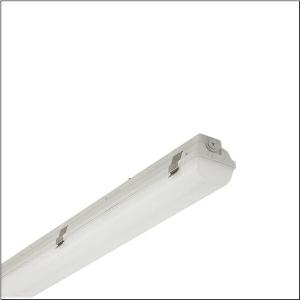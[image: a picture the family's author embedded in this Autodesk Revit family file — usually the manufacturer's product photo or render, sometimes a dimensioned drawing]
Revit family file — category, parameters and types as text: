
# Revit family: monsun_r__21_eco_51fj10ml45a_013e
name_source: partatom
category: Lighting Fixtures
units: mm (PartAtom-declared; Revit-internal decimal feet)

## family parameters
Cut with Voids When Loaded = No
Host = Face
Light Source = No
Part Type = Normal
Room Calculation Point = No
Round Connector Dimension = Use Diameter
Shared = No

## types (1)
- --- (1 x LED, 5000 lm, 36 W, 4000K)
    Apparent Load = 36 VA
    CIE Flux Codes = 41 70 89 90 100
    Color Rendering = 80
    Color Temperature = 4000K
    Default Elevation = 1800 mm
    Description = Monsun® 21 Eco, damp-proof luminaire, primary optical cover: diffuser, of PMMA, frosted, light emission: direct distribution, primary light characteristic: symmetric, installation type: suspended mounting, surface-mounted, LED, rated luminous flux: 5.000lm, luminous efficacy: 139lm/W, light colour: 840, colour temperature: 4000K, control gear: ON/OFF Multilumen, with terminal, 3-pole, max. 2.5mm², mains connection: 220..240V, AC, 50/60Hz, rated input power: 36W, housing, of glass-fibre reinforced polyester, light grey (RAL 7035), length: 1.277mm, width: 90mm, height: 95mm, clip for enclosure, of spring steel V2A, protection rating (complete): IP66, insulation class (complete): insulation class I (protective earthing), certification: CE, UKCA, protection symbol: D, impact resistance: IK02, permissible operating ambient temperature: -20..+35°C, corresponds to IFS (International Featured Standards) requirements for safety and quality in the food industry, contact your sales advisor before using the luminaires in applications with unclear chemical exposure, large temperature fluctuations or condensation-forming humidity, packaging unit: 1 piece
    Height = 103 mm
    Lamp = 1 x LED
    Lamp Light Flux = 5000 lm
    Lamp Power = 36 W
    Lamp count = 1
    Length = 1277 mm
    Luminous efficacy = 139 lm/W
    Manufacturer = Siteco
    ModVariant = No
    Model = 51FJ10ML45A
    Mounting Place = Ceiling
    Mounting Type = Surface mounted
    Number of Poles = 1
    OnlyDefault = Yes
    Power Factor = 1
    Product Name = Monsun® 21 Eco
    Product group = damp-proof luminaire
    ProductGroupID = 301
    Protection Class = Protection class I
    Protection Degree = IP 66
    RLX_Detail_Level = 1
    RLX_Emergency_Light_Flux = 0 lm
    RLX_Emergency_Type = 0
    RLX_Emergency_Type_DB = No
    RlxData = <blob elided: 34057 chars, md5=c035e402>
    Socket = socket
    Standby Power = 0 W
    System Light Flux = 5000 lm
    System Power = 36 W
    Type Comments = factory setting: luminous flux: 100 % | (ON | ON | ON | ON) | 350 mA
    Type Image = l_1007218.jpg
    URL = http://relux.com
    VarID = @adj_149487
    Voltage = 0 V
    Weight = 0.00 kg
    Width = 90 mm

## geometry (parser evidence)
native form markers: Blend x4, Sweep x11
no freeform markers — native parametric forms only
